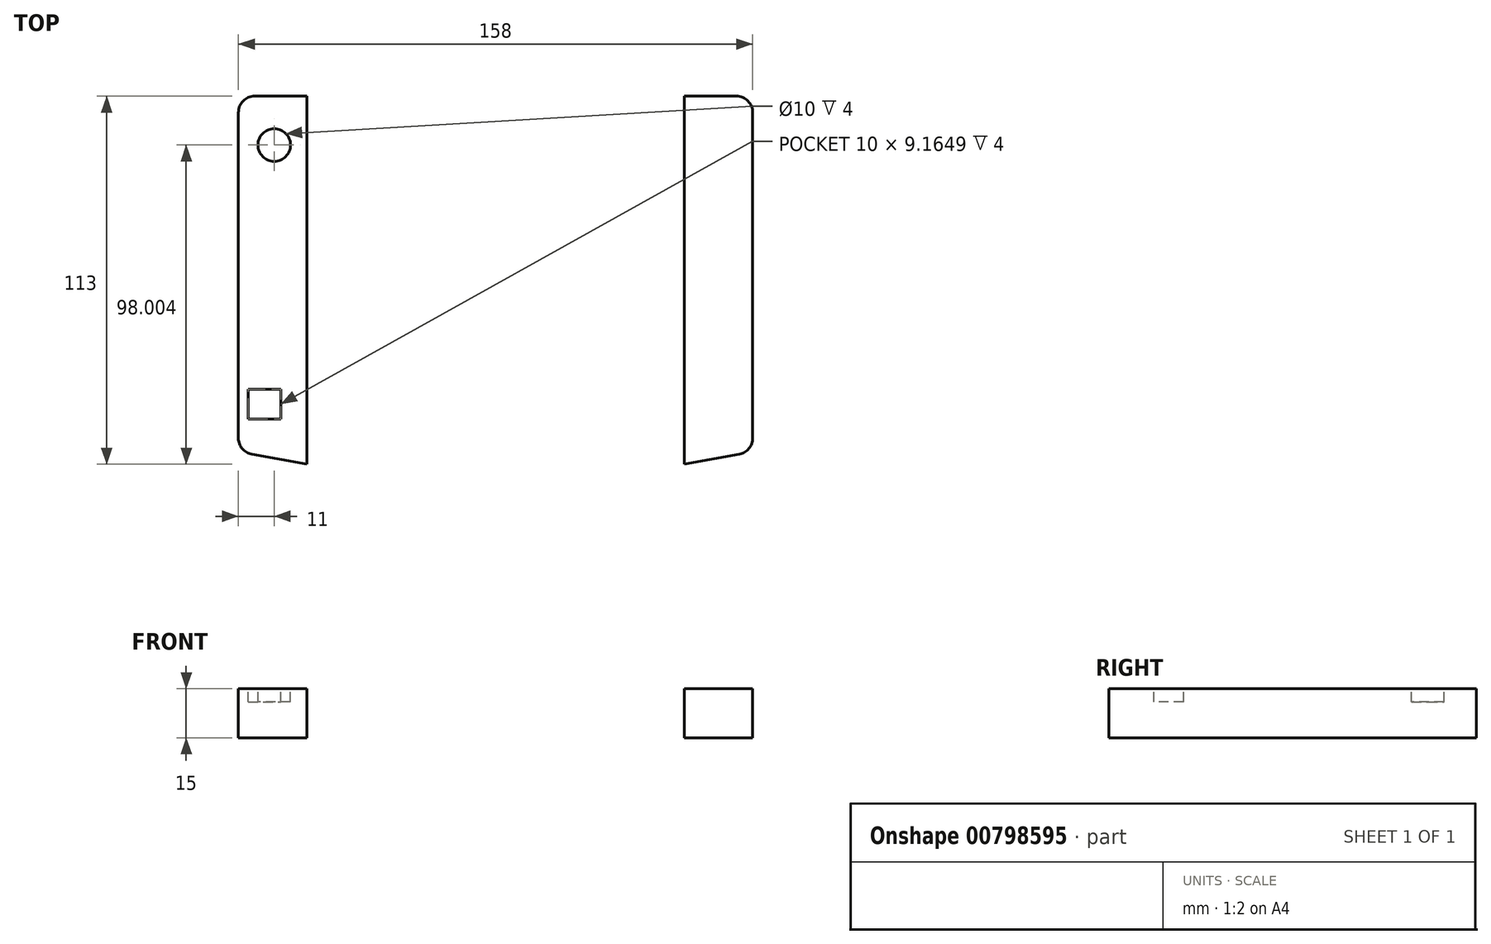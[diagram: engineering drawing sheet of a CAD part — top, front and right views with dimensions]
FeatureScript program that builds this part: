
annotation { "Feature Type Name" : "Feature", "Feature Type Description" : "" }
export const myFeature = defineFeature(function(context is Context, id is Id, definition is map)
    precondition{}
    {
        {
            var Q0;
            Q0=qCreatedBy(makeId("Top.planeOp"),FACE);
            var sketch = newSketch(context, id + "F0", { "sketchPlane" : qUnion([Q0])});
            skLineSegment(sketch, "E0.bottom", {"start": v(58, 72) * mm, "end": v(74, 72) * mm});
            skLineSegment(sketch, "E0.top", {"start": v(58, -38) * mm, "end": v(74, -38) * mm});
            skLineSegment(sketch, "E0.left", {"start": v(58, 72) * mm, "end": v(58, -38) * mm});
            skLineSegment(sketch, "E0.right", {"start": v(79, 67) * mm, "end": v(79, -33) * mm});
            skPoint(sketch, "E1.visualSharp", {"position": v(79, 72) * mm});
            skArc(sketch, "E1.filletArc", {"start": v(79, 67) * mm, "mid": v(77.54, 70.54) * mm, "end": v(74, 72) * mm});
            skPoint(sketch, "E2.visualSharp", {"position": v(79, -38) * mm});
            skArc(sketch, "E2.filletArc", {"start": v(74, -38) * mm, "mid": v(77.54, -36.53) * mm, "end": v(79, -33) * mm});
            skLineSegment(sketch, "E3", {"start": v(58, -38) * mm, "end": v(58, -41) * mm});
            skLineSegment(sketch, "E4", {"start": v(58, -41) * mm, "end": v(74.9, -37.92) * mm});
            skLineSegment(sketch, "E5.MirrorCS", {"start": v(-58, -38) * mm, "end": v(-58, -41) * mm});
            skArc(sketch, "E6.MirrorCS", {"start": v(-79, 67) * mm, "mid": v(-77.54, 70.54) * mm, "end": v(-74, 72) * mm});
            skArc(sketch, "E7.MirrorCS", {"start": v(-74, -38) * mm, "mid": v(-77.54, -36.53) * mm, "end": v(-79, -33) * mm});
            skLineSegment(sketch, "E8.MirrorCS", {"start": v(-58, 72) * mm, "end": v(-74, 72) * mm});
            skLineSegment(sketch, "E9.MirrorCS", {"start": v(-58, -38) * mm, "end": v(-74, -38) * mm});
            skLineSegment(sketch, "E10.MirrorCS", {"start": v(-58, 72) * mm, "end": v(-58, -38) * mm});
            skLineSegment(sketch, "E11.MirrorCS", {"start": v(-58, -41) * mm, "end": v(-74.9, -37.92) * mm});
            skPoint(sketch, "E12.MirrorP", {"position": v(-79, 72) * mm});
            skPoint(sketch, "E13.MirrorP", {"position": v(-79, -38) * mm});
            skLineSegment(sketch, "E14.MirrorCS", {"start": v(-79, 67) * mm, "end": v(-79, -33) * mm});
            skSolve(sketch);
        }
        {
            var Q0;
            Q0 = qSketchRegion(id + "F0", true);
            extrude(context, id + "F1", {"entities" : qUnion([Q0]), "depth" : 15 * mm, "offsetDistance" : 25 * mm});
        }
        {
            var Q0;
            Q0=makeQuery(id+"F1.opExtrude","CAP_FACE",FACE,{"disambiguationData":[OSD([sQuery(id+"F0.wireOp",EDGE,"E5.MirrorCS"),sQuery(id+"F0.wireOp",EDGE,"E6.MirrorCS"),sQuery(id+"F0.wireOp",EDGE,"E7.MirrorCS"),sQuery(id+"F0.wireOp",EDGE,"E8.MirrorCS"),sQuery(id+"F0.wireOp",EDGE,"E10.MirrorCS"),sQuery(id+"F0.wireOp",EDGE,"E11.MirrorCS"),sQuery(id+"F0.wireOp",EDGE,"E14.MirrorCS")])],"isStart":false});
            var sketch = newSketch(context, id + "F2", { "sketchPlane" : qUnion([Q0])});
            skCircle(sketch, "E15", {"center": v(-68, 57) * mm, "radius": 5 * mm});
            skLineSegment(sketch, "E16.bottom", {"start": v(-76, -18) * mm, "end": v(-66, -18) * mm});
            skLineSegment(sketch, "E16.top", {"start": v(-76, -27.16) * mm, "end": v(-66, -27.16) * mm});
            skLineSegment(sketch, "E16.left", {"start": v(-76, -18) * mm, "end": v(-76, -27.16) * mm});
            skLineSegment(sketch, "E16.right", {"start": v(-66, -18) * mm, "end": v(-66, -27.16) * mm});
            skSolve(sketch);
        }
        {
            var Q0;
            Q0 = qSketchRegion(id + "F2", true);
            extrude(context, id + "F3", {"entities" : qUnion([Q0]), "operationType" : NewBodyOperationType.REMOVE, "oppositeDirection" : true, "depth" : 4 * mm, "offsetDistance" : 25 * mm});
        }
    });
